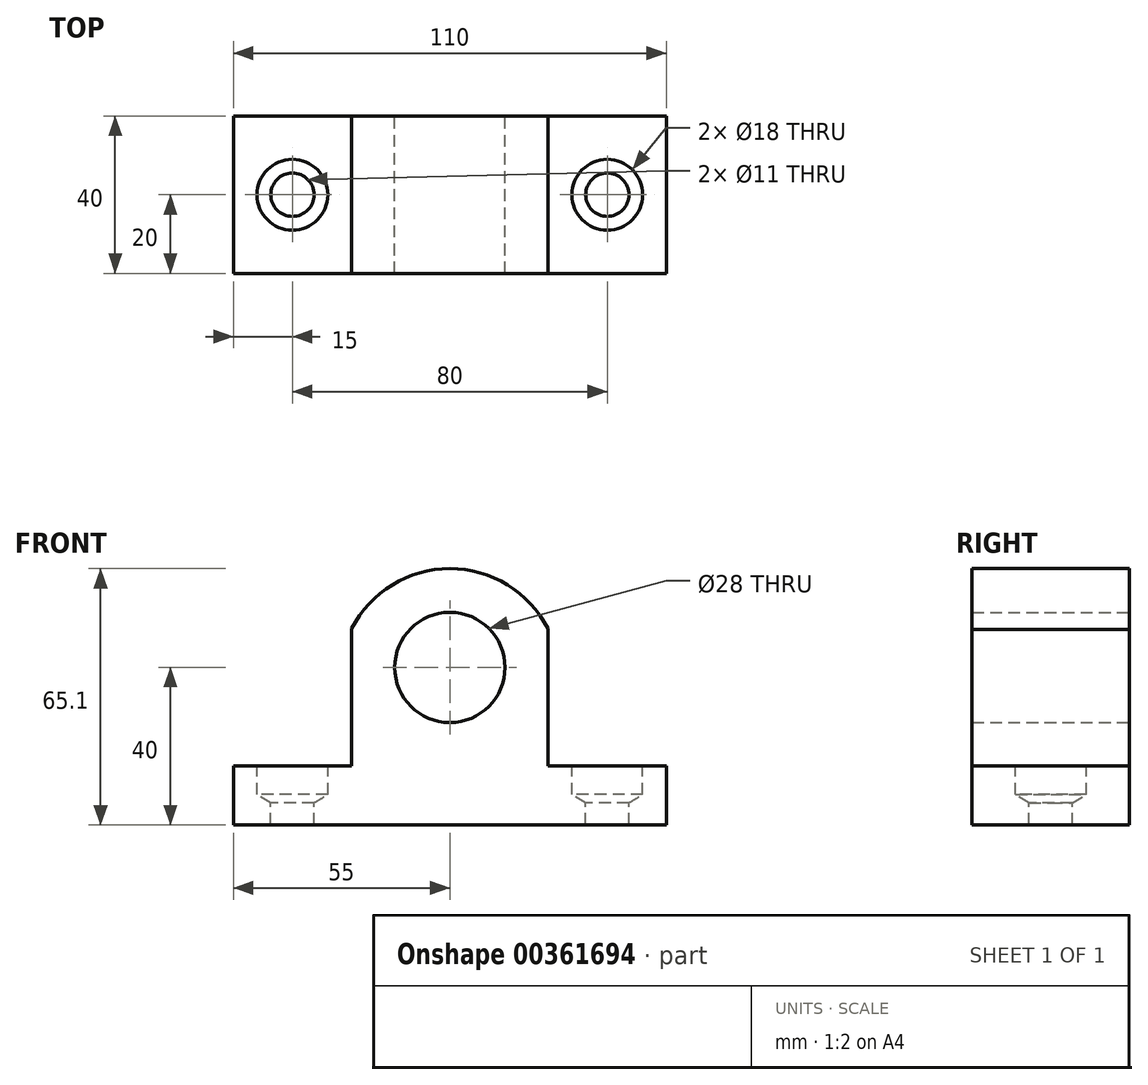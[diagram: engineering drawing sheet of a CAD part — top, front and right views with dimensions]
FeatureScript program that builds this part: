
annotation { "Feature Type Name" : "Feature", "Feature Type Description" : "" }
export const myFeature = defineFeature(function(context is Context, id is Id, definition is map)
    precondition{}
    {
        {
            var Q0;
            Q0=qCreatedBy(makeId("Front.planeOp"),FACE);
            var sketch = newSketch(context, id + "F0", { "sketchPlane" : qUnion([Q0])});
            skLineSegment(sketch, "E0", {"start": v(-55, 0) * mm, "end": v(55, 0) * mm});
            skLineSegment(sketch, "E1", {"start": v(55, 0) * mm, "end": v(55, 15) * mm});
            skLineSegment(sketch, "E2", {"start": v(55, 15) * mm, "end": v(25, 15) * mm});
            skLineSegment(sketch, "E3", {"start": v(25, 15) * mm, "end": v(25, 49.72) * mm});
            skLineSegment(sketch, "E4", {"start": v(25, 49.72) * mm, "end": v(24.93, 49.86) * mm});
            skLineSegment(sketch, "E5", {"start": v(-24.93, 49.86) * mm, "end": v(-25, 49.72) * mm});
            skLineSegment(sketch, "E6", {"start": v(-25, 49.72) * mm, "end": v(-25, 15) * mm});
            skLineSegment(sketch, "E7", {"start": v(-25, 15) * mm, "end": v(-55, 15) * mm});
            skLineSegment(sketch, "E8", {"start": v(-55, 15) * mm, "end": v(-55, 0) * mm});
            skCircle(sketch, "E9", {"center": v(0, 40) * mm, "radius": 14 * mm});
            skPoint(sketch, "E10.visualSharp", {"position": v(0, 98.59) * mm});
            skArc(sketch, "E10.filletArc", {"start": v(24.93, 49.86) * mm, "mid": v(0, 65.1) * mm, "end": v(-24.93, 49.86) * mm});
            skSolve(sketch);
        }
        {
            var Q0;
            Q0=makeQuery(id+"F0.imprint","IMPRINT",FACE,{"disambiguationData":[TD([[makeQuery(id+"F0.imprint","IMPRINT",EDGE,{"derivedFrom":sQuery(id+"F0.wireOp",EDGE,"E0")}),1.0]])]});
            extrude(context, id + "F1", {"entities" : qUnion([Q0]), "depth" : 40 * mm, "offsetDistance" : 25 * mm});
        }
        {
            var Q0;
            Q0=makeQuery(id+"F1.opExtrude","SWEPT_FACE",FACE,{"disambiguationData":[OSD([sQuery(id+"F0.wireOp",EDGE,"E7")])]});
            var sketch = newSketch(context, id + "F2", { "sketchPlane" : qUnion([Q0])});
            skCircle(sketch, "E11", {"center": v(-40, -20) * mm, "radius": 9 * mm});
            skCircle(sketch, "E12", {"center": v(40, -20) * mm, "radius": 9 * mm});
            skSolve(sketch);
        }
        {
            var Q0;
            Q0=sQuery(id+"F2.wireOp",VERTEX,"E11.center");
            var Q1;
            Q1=sQuery(id+"F2.wireOp",VERTEX,"E12.center");
            var Q2;
            Q2=makeQuery(id+"F1.opExtrude","SWEPT_BODY",BODY,{"disambiguationData":[OSD([sQuery(id+"F0.wireOp",EDGE,"E0"),sQuery(id+"F0.wireOp",EDGE,"E1"),sQuery(id+"F0.wireOp",EDGE,"E2"),sQuery(id+"F0.wireOp",EDGE,"E3"),sQuery(id+"F0.wireOp",EDGE,"E4"),sQuery(id+"F0.wireOp",EDGE,"E5"),sQuery(id+"F0.wireOp",EDGE,"E6"),sQuery(id+"F0.wireOp",EDGE,"E7"),sQuery(id+"F0.wireOp",EDGE,"E8"),sQuery(id+"F0.wireOp",EDGE,"E9"),sQuery(id+"F0.wireOp",EDGE,"E10.filletArc")])]});
            hole(context, id + "F3", {"style" : HoleStyle.SIMPLE, "endStyle" : HoleEndStyle.BLIND, "holeDiameter" : 18 * mm, "holeDepth" : 7.3 * mm, "isTappedThrough" : true, "tappedDepth" : 12 * mm, "tapClearance" : 3, "startFromSketch" : true, "locations" : qUnion([Q0, Q1]), "scope" : qUnion([Q2])});
        }
        {
            var Q0;
            Q0=sQuery(id+"F2.wireOp",VERTEX,"E11.center");
            var Q1;
            Q1=sQuery(id+"F2.wireOp",VERTEX,"E12.center");
            var Q2;
            Q2=makeQuery(id+"F1.opExtrude","SWEPT_BODY",BODY,{"disambiguationData":[OSD([sQuery(id+"F0.wireOp",EDGE,"E0"),sQuery(id+"F0.wireOp",EDGE,"E1"),sQuery(id+"F0.wireOp",EDGE,"E2"),sQuery(id+"F0.wireOp",EDGE,"E3"),sQuery(id+"F0.wireOp",EDGE,"E4"),sQuery(id+"F0.wireOp",EDGE,"E5"),sQuery(id+"F0.wireOp",EDGE,"E6"),sQuery(id+"F0.wireOp",EDGE,"E7"),sQuery(id+"F0.wireOp",EDGE,"E8"),sQuery(id+"F0.wireOp",EDGE,"E9"),sQuery(id+"F0.wireOp",EDGE,"E10.filletArc")])]});
            hole(context, id + "F4", {"style" : HoleStyle.SIMPLE, "endStyle" : HoleEndStyle.BLIND, "holeDiameter" : 11 * mm, "holeDepth" : 15 * mm, "isTappedThrough" : true, "tappedDepth" : 12 * mm, "tapClearance" : 3, "startFromSketch" : true, "locations" : qUnion([Q0, Q1]), "scope" : qUnion([Q2])});
        }
    });
